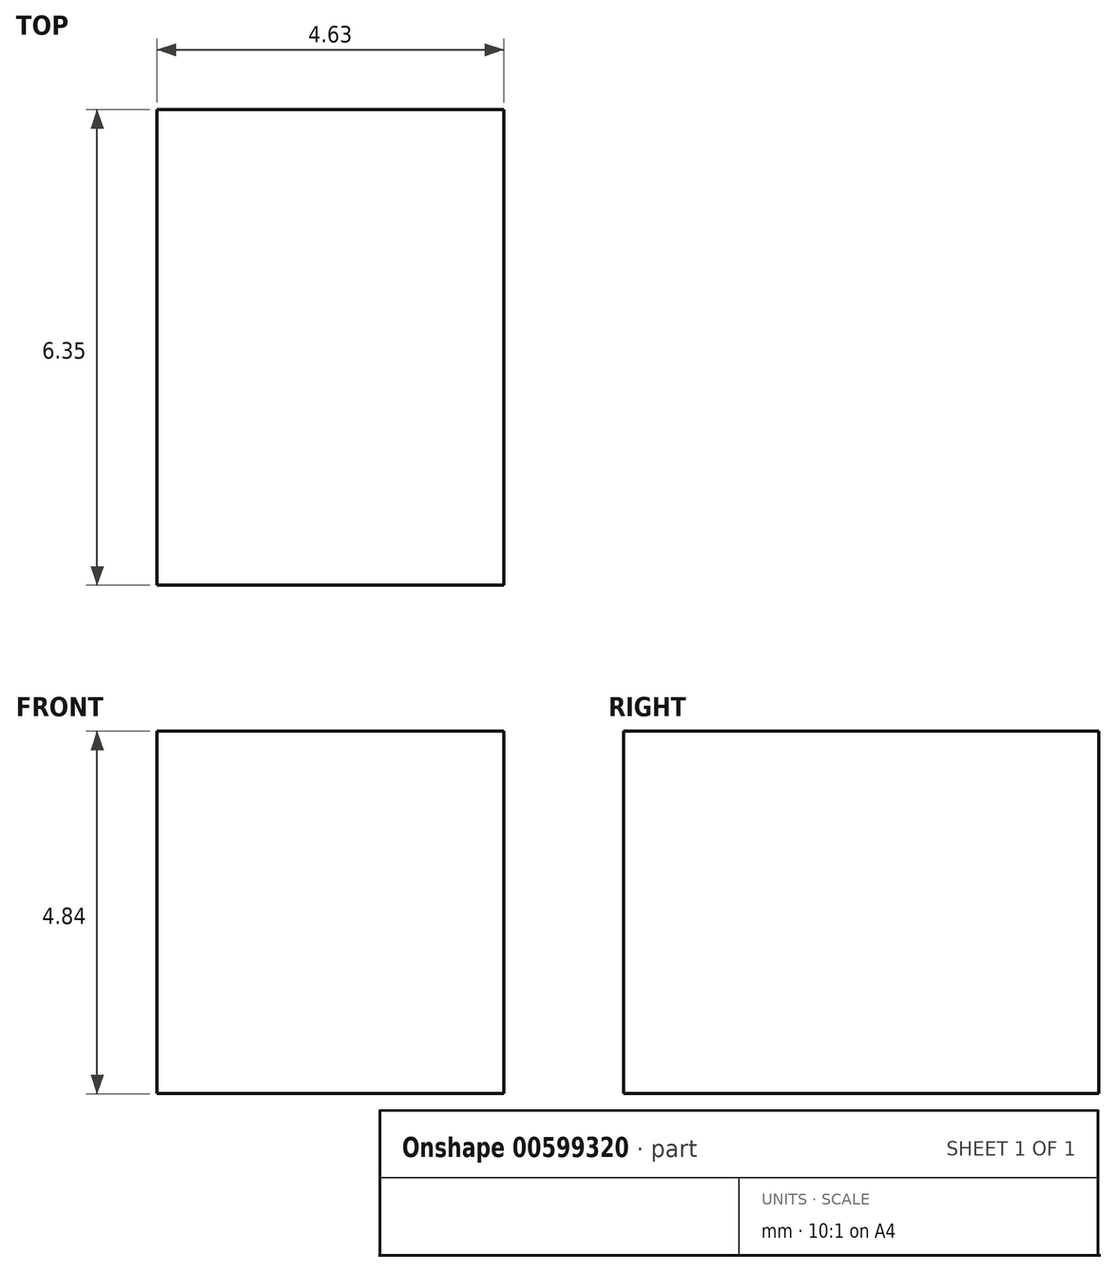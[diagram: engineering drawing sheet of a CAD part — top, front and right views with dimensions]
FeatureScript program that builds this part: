
annotation { "Feature Type Name" : "Feature", "Feature Type Description" : "" }
export const myFeature = defineFeature(function(context is Context, id is Id, definition is map)
    precondition{}
    {
        {
            var Q0;
            Q0=qCreatedBy(makeId("Front.planeOp"),FACE);
            var sketch = newSketch(context, id + "F0", { "sketchPlane" : qUnion([Q0])});
            skLineSegment(sketch, "E0.bottom", {"start": v(11.07, 30.22) * mm, "end": v(15.7, 30.22) * mm});
            skLineSegment(sketch, "E0.top", {"start": v(11.07, 25.38) * mm, "end": v(15.7, 25.38) * mm});
            skLineSegment(sketch, "E0.left", {"start": v(11.07, 30.22) * mm, "end": v(11.07, 25.38) * mm});
            skLineSegment(sketch, "E0.right", {"start": v(15.7, 30.22) * mm, "end": v(15.7, 25.38) * mm});
            skSolve(sketch);
        }
        {
            var Q0;
            Q0 = qSketchRegion(id + "F0", true);
            extrude(context, id + "F1", {"entities" : qUnion([Q0]), "depth" : 6.35 * mm, "offsetDistance" : 25.4 * mm});
        }
    });
